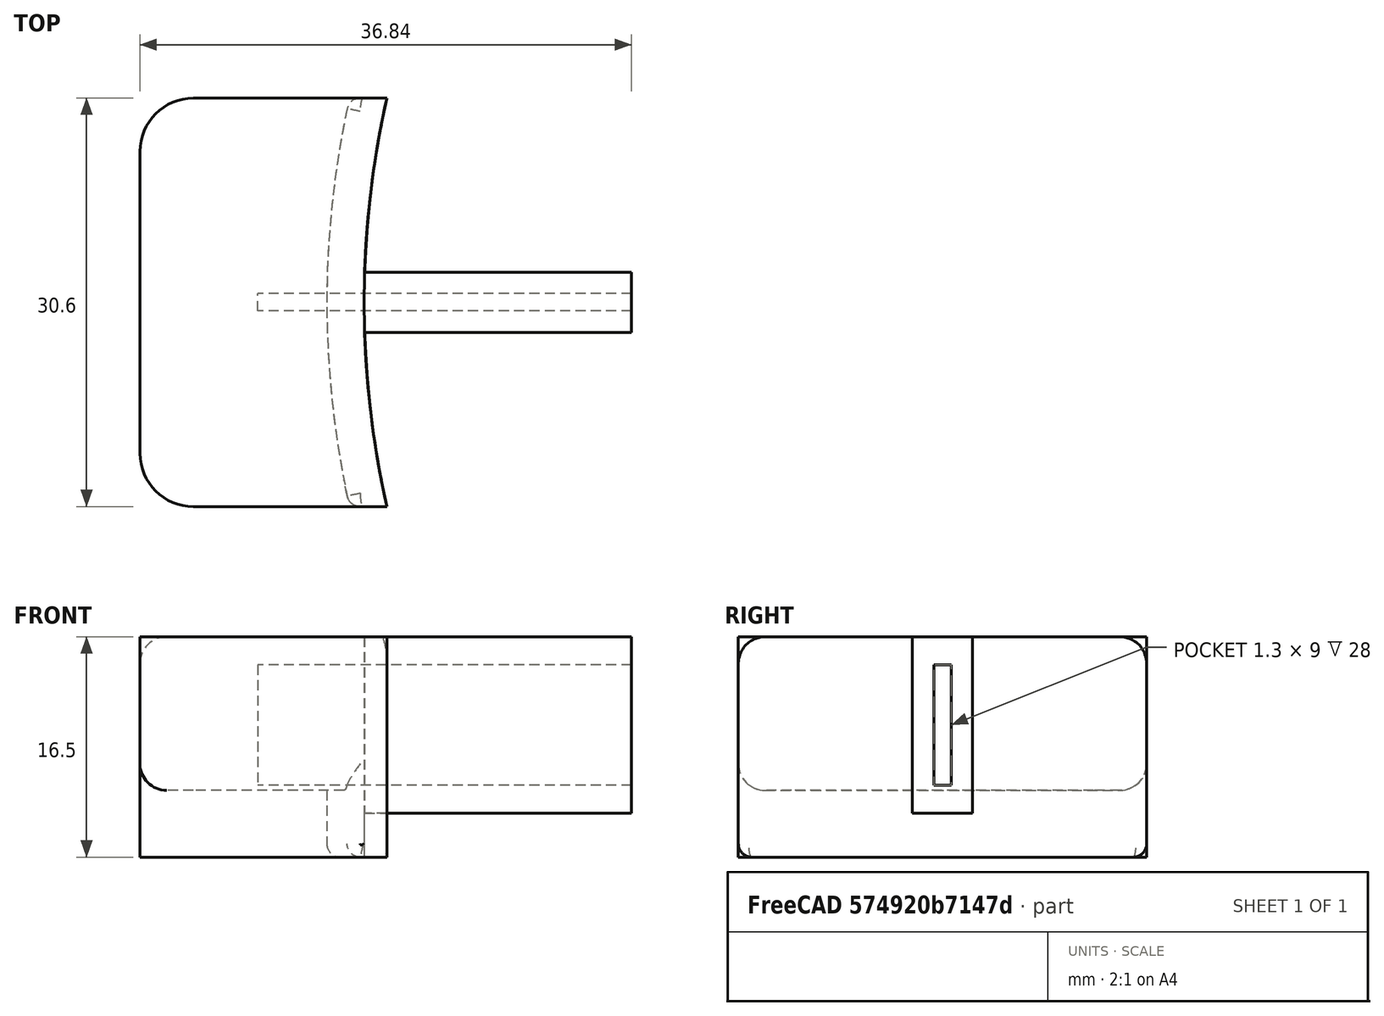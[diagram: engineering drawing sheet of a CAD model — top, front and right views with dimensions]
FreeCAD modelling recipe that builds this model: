
FCSTD DOCUMENT  (FreeCAD 0.16R6712 (Git))
Label: Bouton Grille Pain
License: All rights reserved
LicenseURL: http://en.wikipedia.org/wiki/All_rights_reserved
objects: Sketcher::SketchObject×4, PartDesign::Fillet×3, PartDesign::Pad×2, PartDesign::Pocket×2, Mesh::Feature×1
note: 15 computed .brp shape members not serialized (recipe doc carries the construction recipe); baked Part::Feature solids carry a one-line shape summary decoded from their .brp

FEATURE [Sketcher::SketchObject] Sketch
  sketch-geometry (7):
    g0: LineSegment StartX=18.5 StartY=15.3 StartZ=0 EndX=4 EndY=15.3 EndZ=0
    g1: LineSegment StartX=0 StartY=11.3 StartZ=0 EndX=0 EndY=-11.3 EndZ=0
    g2: LineSegment StartX=4 StartY=-15.3 StartZ=0 EndX=18.5 EndY=-15.3 EndZ=0
    g3: ArcOfCircle CenterX=86.5 CenterY=0 CenterZ=0 NormalX=0 NormalY=0 NormalZ=1 Radius=69.7 StartAngle=2.92028 EndAngle=3.36291
    g4: ArcOfCircle CenterX=4 CenterY=-11.3 CenterZ=0 NormalX=0 NormalY=0 NormalZ=1 Radius=4 StartAngle=3.14159 EndAngle=4.71239
    g5: ArcOfCircle CenterX=4 CenterY=11.3 CenterZ=0 NormalX=0 NormalY=0 NormalZ=1 Radius=4 StartAngle=1.5708 EndAngle=3.14159
    g6: GeomPoint [constr] X=16.8 Y=0 Z=0
  constraints (19):
    c: Horizontal(g0)
    c: Horizontal(g2)
    c: PointOnObject(g3,g-1)
    c: Coincident(g3,g0)
    c: Coincident(g3,g2)
    c: Tangent(g2,g4) = -1.5708
    c: Tangent(g1,g4) = -1.5708
    c: Tangent(g0,g5) = -1.5708
    c: Tangent(g1,g5) = -1.5708
    c: DistanceY(g2,g0) = 30.6
    c: DistanceX(g1,g2) = 4
    c: Equal(g5,g4)
    c: Vertical(g1)
    c: PointOnObject(g-1,g1)
    c: Symmetric(g1,g1,g-1)
    c: DistanceX(g1,g0) = 18.5
    c: PointOnObject(g6,g-1)
    c: PointOnObject(g6,g3)
    c: DistanceX(g-1,g6) = 16.8
FEATURE [PartDesign::Pad] Pad
  Length = 16.5
  Length2 = 100
  Sketch = -> Sketch
  Type = 0
FEATURE [Sketcher::SketchObject] Sketch001
  ExternalGeometry = -> [Pad]
  Placement = pos=(0,0,16.5) rot=(0,0,1;0rad)
  Support = -> Pad [Face8]
  sketch-geometry (5):
    g0: LineSegment StartX=0 StartY=2.25 StartZ=0 EndX=36.8363 EndY=2.25 EndZ=0
    g1: LineSegment StartX=36.8363 StartY=2.25 StartZ=0 EndX=36.8363 EndY=-2.25 EndZ=0
    g2: LineSegment StartX=36.8363 StartY=-2.25 StartZ=0 EndX=0 EndY=-2.25 EndZ=0
    g3: LineSegment StartX=0 StartY=-2.25 StartZ=0 EndX=0 EndY=2.25 EndZ=0
    g4: GeomPoint [constr] X=16.8363 Y=2.25 Z=0
  constraints (14):
    c: Coincident(g0,g1)
    c: Coincident(g1,g2)
    c: Coincident(g2,g3)
    c: Coincident(g3,g0)
    c: Horizontal(g0)
    c: Horizontal(g2)
    c: Vertical(g1)
    c: Vertical(g3)
    c: PointOnObject(g0,g-3)
    c: Symmetric(g0,g2,g-1)
    c: DistanceY(g1,g0) = 4.5
    c: PointOnObject(g4,g-4)
    c: PointOnObject(g4,g0)
    c: DistanceX(g4,g0) = 20
FEATURE [PartDesign::Pad] Pad001
  Length = 13.2
  Length2 = 100
  Reversed = true
  Sketch = -> Sketch001
  Type = 0
FEATURE [Sketcher::SketchObject] Sketch002
  ExternalGeometry = -> [Pad001]
  Placement = pos=(36.8363,0,0) rot=(0.57735,0.57735,0.57735;2.0944rad)
  Support = -> Pad001 [Face15]
  sketch-geometry (8):
    g0: LineSegment StartX=-0.65 StartY=14.4 StartZ=0 EndX=0.65 EndY=14.4 EndZ=0
    g1: LineSegment StartX=0.65 StartY=14.4 StartZ=0 EndX=0.65 EndY=5.4 EndZ=0
    g2: LineSegment StartX=0.65 StartY=5.4 StartZ=0 EndX=-0.65 EndY=5.4 EndZ=0
    g3: LineSegment StartX=-0.65 StartY=5.4 StartZ=0 EndX=-0.65 EndY=14.4 EndZ=0
    g4: LineSegment [constr] StartX=-0.65 StartY=14.4 StartZ=0 EndX=-2.25 EndY=14.4 EndZ=0
    g5: LineSegment [constr] StartX=0.65 StartY=14.4 StartZ=0 EndX=2.25 EndY=14.4 EndZ=0
    g6: LineSegment [constr] StartX=-0.65 StartY=14.4 StartZ=0 EndX=-0.65 EndY=16.5 EndZ=0
    g7: LineSegment [constr] StartX=-0.65 StartY=5.4 StartZ=0 EndX=-0.65 EndY=3.3 EndZ=0
  constraints (24):
    c: Coincident(g0,g1)
    c: Coincident(g1,g2)
    c: Coincident(g2,g3)
    c: Coincident(g3,g0)
    c: Horizontal(g0)
    c: Horizontal(g2)
    c: Vertical(g1)
    c: Vertical(g3)
    c: DistanceX(g0,g0) = 1.3
    c: DistanceY(g1,g0) = 9
    c: Coincident(g4,g0)
    c: PointOnObject(g4,g-3)
    c: Horizontal(g4)
    c: Coincident(g5,g0)
    c: PointOnObject(g5,g-4)
    c: Horizontal(g5)
    c: Equal(g5,g4)
    c: Coincident(g6,g0)
    c: PointOnObject(g6,g-5)
    c: Vertical(g6)
    c: Coincident(g7,g2)
    c: PointOnObject(g7,g-6)
    c: Vertical(g7)
    c: Equal(g6,g7)
FEATURE [PartDesign::Pocket] Pocket
  Length = 28
  Sketch = -> Sketch002
  Type = 0
FEATURE [Sketcher::SketchObject] Sketch003
  ExternalGeometry = -> [Pocket]
  Placement = pos=(0,0,0) rot=(1,0,0;3.14159rad)
  Support = -> Pocket [Face4]
  sketch-geometry (8):
    g0: LineSegment StartX=0 StartY=15.3 StartZ=0 EndX=0 EndY=-15.3 EndZ=0
    g1: GeomPoint [constr] X=16.8 Y=0 Z=0
    g2: LineSegment [constr] StartX=18.5 StartY=15.3 StartZ=0 EndX=15.7 EndY=15.3 EndZ=0
    g3: LineSegment [constr] StartX=16.8 StartY=0 StartZ=0 EndX=14 EndY=0 EndZ=0
    g4: LineSegment [constr] StartX=18.5 StartY=-15.3 StartZ=0 EndX=15.7 EndY=-15.3 EndZ=0
    g5: ArcOfCircle CenterX=83.7 CenterY=1e-12 CenterZ=0 NormalX=0 NormalY=0 NormalZ=1 Radius=69.7 StartAngle=2.92028 EndAngle=3.36291
    g6: LineSegment StartX=0 StartY=15.3 StartZ=0 EndX=15.7 EndY=15.3 EndZ=0
    g7: LineSegment StartX=0 StartY=-15.3 StartZ=0 EndX=15.7 EndY=-15.3 EndZ=0
  constraints (22):
    c: PointOnObject(g0,g-2)
    c: Vertical(g0)
    c: PointOnObject(g1,g-1)
    c: PointOnObject(g1,g-3)
    c: Coincident(g2,g-3)
    c: Horizontal(g2)
    c: DistanceX(g2,g2) = 2.8
    c: Coincident(g3,g1)
    c: Horizontal(g3)
    c: Coincident(g4,g-3)
    c: Horizontal(g4)
    c: Equal(g4,g3)
    c: Equal(g3,g2)
    c: Coincident(g5,g4)
    c: Coincident(g5,g2)
    c: PointOnObject(g3,g5)
    c: Coincident(g6,g0)
    c: Coincident(g6,g2)
    c: Horizontal(g6)
    c: Coincident(g7,g0)
    c: Coincident(g7,g4)
    c: Horizontal(g7)
FEATURE [PartDesign::Pocket] Pocket001
  Length = 5
  Sketch = -> Sketch003
  Type = 0
FEATURE [PartDesign::Fillet] Fillet
  Base = -> Pocket001 [Edge7]
  Radius = 1
FEATURE [PartDesign::Fillet] Fillet001
  Base = -> Fillet [Edge4,Edge2,Edge1,Edge19,Edge11,Edge10]
  Radius = 1
FEATURE [PartDesign::Fillet] Fillet002
  Base = -> Fillet001 [Edge34,Edge45,Edge52,Edge35,Edge51,Edge61,Edge22,Edge37,Edge38,Edge36,Edge26,Edge7,Edge3,Edge21]
  Radius = 2
FEATURE [Mesh::Feature] Mesh  label="Fillet002 (Meshed)"
